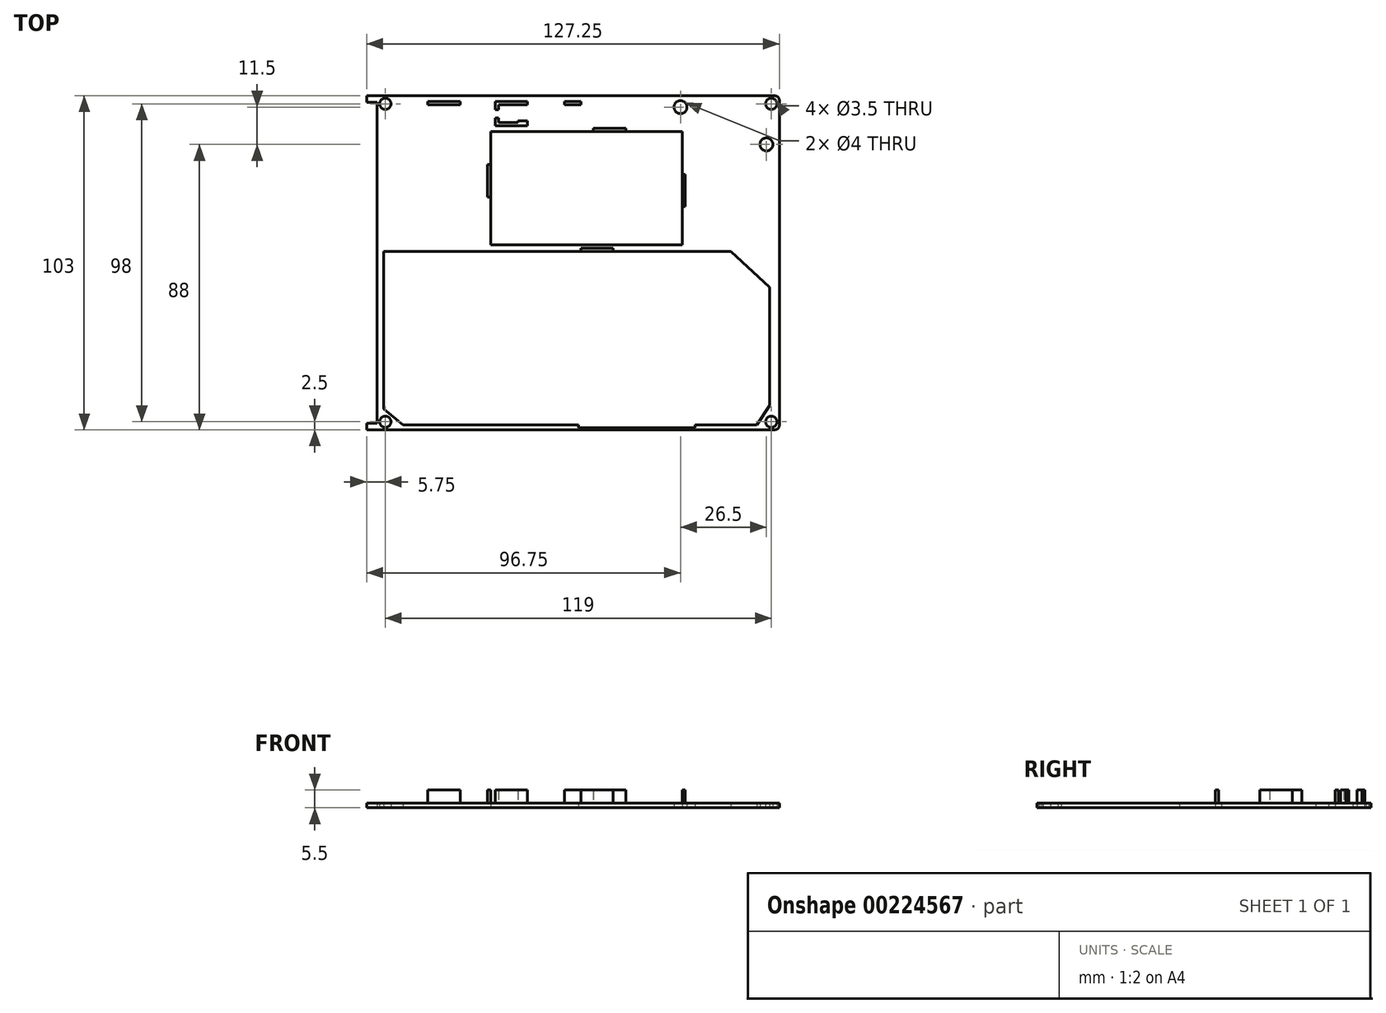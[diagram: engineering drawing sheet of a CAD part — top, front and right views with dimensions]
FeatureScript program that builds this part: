
annotation { "Feature Type Name" : "Feature", "Feature Type Description" : "" }
export const myFeature = defineFeature(function(context is Context, id is Id, definition is map)
    precondition{}
    {
        {
            var Q0;
            Q0=qCreatedBy(makeId("Top.planeOp"),FACE);
            var sketch = newSketch(context, id + "F0", { "sketchPlane" : qUnion([Q0])});
            skLineSegment(sketch, "E0.bottom", {"start": v(-1.5, 0) * mm, "end": v(-122.5, 0) * mm});
            skLineSegment(sketch, "E0.top", {"start": v(-1.5, 103) * mm, "end": v(-122.5, 103) * mm});
            skLineSegment(sketch, "E0.left", {"start": v(0, 1.5) * mm, "end": v(0, 101.5) * mm});
            skLineSegment(sketch, "E0.right", {"start": v(-124, 2) * mm, "end": v(-124, 101) * mm});
            skLineSegment(sketch, "E1.bottom", {"start": v(-7, 1.5) * mm, "end": v(-116, 1.5) * mm});
            skLineSegment(sketch, "E1.top", {"start": v(-30, 92) * mm, "end": v(-89, 92) * mm});
            skLineSegment(sketch, "E1.left", {"start": v(-3, 7.5) * mm, "end": v(-3, 44) * mm});
            skLineSegment(sketch, "E1.right", {"start": v(-122, 6.5) * mm, "end": v(-122, 55) * mm});
            skLineSegment(sketch, "E2", {"start": v(-116, 1.5) * mm, "end": v(-122, 6.5) * mm});
            skLineSegment(sketch, "E3", {"start": v(-7, 1.5) * mm, "end": v(-3, 7.5) * mm});
            skLineSegment(sketch, "E4", {"start": v(-3, 44) * mm, "end": v(-15, 55) * mm});
            skLineSegment(sketch, "E5", {"start": v(-15, 55) * mm, "end": v(-30, 55) * mm});
            skLineSegment(sketch, "E6", {"start": v(-30, 57) * mm, "end": v(-30, 92) * mm});
            skLineSegment(sketch, "E7", {"start": v(-30, 55) * mm, "end": v(-122, 55) * mm});
            skLineSegment(sketch, "E8", {"start": v(-30, 57) * mm, "end": v(-89, 57) * mm});
            skLineSegment(sketch, "E9", {"start": v(-89, 92) * mm, "end": v(-89, 57) * mm});
            skCircle(sketch, "E10", {"center": v(-2.5, 100.5) * mm, "radius": 1.75 * mm});
            skCircle(sketch, "E11", {"center": v(-121.5, 100.5) * mm, "radius": 1.75 * mm});
            skCircle(sketch, "E12", {"center": v(-121.5, 2.5) * mm, "radius": 1.75 * mm});
            skCircle(sketch, "E13", {"center": v(-2.5, 2.5) * mm, "radius": 1.75 * mm});
            skCircle(sketch, "E14", {"center": v(-4, 88) * mm, "radius": 2 * mm});
            skCircle(sketch, "E15", {"center": v(-30.5, 99.5) * mm, "radius": 2 * mm});
            skPoint(sketch, "E16.visualSharp", {"position": v(0, 103) * mm});
            skArc(sketch, "E16.filletArc", {"start": v(0, 101.5) * mm, "mid": v(-0.44, 102.56) * mm, "end": v(-1.5, 103) * mm});
            skPoint(sketch, "E17.visualSharp", {"position": v(0, 0) * mm});
            skArc(sketch, "E17.filletArc", {"start": v(-1.5, 0) * mm, "mid": v(-0.44, 0.44) * mm, "end": v(0, 1.5) * mm});
            skLineSegment(sketch, "E18", {"start": v(-26, 1.5) * mm, "end": v(-26, 0.7) * mm});
            skLineSegment(sketch, "E19", {"start": v(-26, 0.7) * mm, "end": v(-62, 0.7) * mm});
            skLineSegment(sketch, "E20", {"start": v(-62, 0.7) * mm, "end": v(-62, 1.5) * mm});
            skLineSegment(sketch, "E21", {"start": v(-124, 2) * mm, "end": v(-127.25, 2) * mm});
            skLineSegment(sketch, "E22", {"start": v(-127.25, 2) * mm, "end": v(-127.25, 0) * mm});
            skLineSegment(sketch, "E23", {"start": v(-127.25, 0) * mm, "end": v(-122.5, 0) * mm});
            skLineSegment(sketch, "E24", {"start": v(-122.5, 103) * mm, "end": v(-127.25, 103) * mm});
            skLineSegment(sketch, "E25", {"start": v(-124, 101) * mm, "end": v(-127.25, 101) * mm});
            skLineSegment(sketch, "E26", {"start": v(-127.25, 101) * mm, "end": v(-127.25, 103) * mm});
            skSolve(sketch);
        }
        {
            var Q0;
            Q0 = qSketchRegion(id + "F0", true);
            extrude(context, id + "F1", {"entities" : qUnion([Q0]), "depth" : 1.5 * mm});
        }
        {
            var Q0;
            Q0=makeQuery(id+"F1.opExtrude","CAP_FACE",FACE,{"disambiguationData":[OSD([sQuery(id+"F0.wireOp",EDGE,"E0.bottom"),sQuery(id+"F0.wireOp",EDGE,"E0.top"),sQuery(id+"F0.wireOp",EDGE,"E0.left"),sQuery(id+"F0.wireOp",EDGE,"E0.right"),sQuery(id+"F0.wireOp",EDGE,"E1.bottom"),sQuery(id+"F0.wireOp",EDGE,"E1.top"),sQuery(id+"F0.wireOp",EDGE,"E1.left"),sQuery(id+"F0.wireOp",EDGE,"E1.right"),sQuery(id+"F0.wireOp",EDGE,"E2"),sQuery(id+"F0.wireOp",EDGE,"E3"),sQuery(id+"F0.wireOp",EDGE,"E4"),sQuery(id+"F0.wireOp",EDGE,"E5"),sQuery(id+"F0.wireOp",EDGE,"E6"),sQuery(id+"F0.wireOp",EDGE,"E7"),sQuery(id+"F0.wireOp",EDGE,"E8"),sQuery(id+"F0.wireOp",EDGE,"E9"),sQuery(id+"F0.wireOp",EDGE,"E10"),sQuery(id+"F0.wireOp",EDGE,"E11"),sQuery(id+"F0.wireOp",EDGE,"E12"),sQuery(id+"F0.wireOp",EDGE,"E13"),sQuery(id+"F0.wireOp",EDGE,"E14"),sQuery(id+"F0.wireOp",EDGE,"E15"),sQuery(id+"F0.wireOp",EDGE,"E16.filletArc"),sQuery(id+"F0.wireOp",EDGE,"E17.filletArc"),sQuery(id+"F0.wireOp",EDGE,"009ea5dd-0bb8-4e20-ba9f-81f578676786.filletArc"),sQuery(id+"F0.wireOp",EDGE,"e55fcb94-b343-4f6b-ae36-d151259c01dc.filletArc"),sQuery(id+"F0.wireOp",EDGE,"E18"),sQuery(id+"F0.wireOp",EDGE,"E19"),sQuery(id+"F0.wireOp",EDGE,"E20")])],"isStart":false});
            var sketch = newSketch(context, id + "F2", { "sketchPlane" : qUnion([Q0])});
            skLineSegment(sketch, "E27.bottom", {"start": v(-87.63, 101.2) * mm, "end": v(-77.63, 101.2) * mm});
            skLineSegment(sketch, "E27.top", {"start": v(-86.63, 100.2) * mm, "end": v(-77.63, 100.2) * mm});
            skLineSegment(sketch, "E27.left", {"start": v(-87.63, 101.2) * mm, "end": v(-87.63, 100.2) * mm});
            skLineSegment(sketch, "E27.right", {"start": v(-77.63, 101.2) * mm, "end": v(-77.63, 100.2) * mm});
            skLineSegment(sketch, "E28.top", {"start": v(-87.63, 98.7) * mm, "end": v(-86.63, 98.7) * mm});
            skLineSegment(sketch, "E28.left", {"start": v(-87.63, 100.2) * mm, "end": v(-87.63, 98.7) * mm});
            skLineSegment(sketch, "E28.right", {"start": v(-86.63, 100.2) * mm, "end": v(-86.63, 98.7) * mm});
            skLineSegment(sketch, "E29.bottom", {"start": v(-87.63, 96.2) * mm, "end": v(-86.63, 96.2) * mm});
            skLineSegment(sketch, "E29.left", {"start": v(-87.63, 96.2) * mm, "end": v(-87.63, 94.7) * mm});
            skLineSegment(sketch, "E29.right", {"start": v(-86.63, 96.2) * mm, "end": v(-86.63, 94.7) * mm});
            skLineSegment(sketch, "E30.bottom", {"start": v(-86.63, 94.7) * mm, "end": v(-80.63, 94.7) * mm});
            skLineSegment(sketch, "E30.top", {"start": v(-87.63, 93.7) * mm, "end": v(-77.63, 93.7) * mm});
            skLineSegment(sketch, "E30.left", {"start": v(-87.63, 94.7) * mm, "end": v(-87.63, 93.7) * mm});
            skLineSegment(sketch, "E30.right", {"start": v(-77.63, 94.7) * mm, "end": v(-77.63, 93.7) * mm});
            skLineSegment(sketch, "E31.top", {"start": v(-77.63, 95.25) * mm, "end": v(-80.63, 95.25) * mm});
            skLineSegment(sketch, "E31.left", {"start": v(-77.63, 94.7) * mm, "end": v(-77.63, 95.25) * mm});
            skLineSegment(sketch, "E31.right", {"start": v(-80.63, 94.7) * mm, "end": v(-80.63, 95.25) * mm});
            skLineSegment(sketch, "E32.bottom", {"start": v(-89, 81.76) * mm, "end": v(-90, 81.76) * mm});
            skLineSegment(sketch, "E32.top", {"start": v(-89, 71.76) * mm, "end": v(-90, 71.76) * mm});
            skLineSegment(sketch, "E32.left", {"start": v(-89, 81.76) * mm, "end": v(-89, 71.76) * mm});
            skLineSegment(sketch, "E32.right", {"start": v(-90, 81.76) * mm, "end": v(-90, 71.76) * mm});
            skLineSegment(sketch, "E33.bottom", {"start": v(-61.21, 55) * mm, "end": v(-51.21, 55) * mm});
            skLineSegment(sketch, "E33.top", {"start": v(-61.21, 56) * mm, "end": v(-51.21, 56) * mm});
            skLineSegment(sketch, "E33.left", {"start": v(-61.21, 55) * mm, "end": v(-61.21, 56) * mm});
            skLineSegment(sketch, "E33.right", {"start": v(-51.21, 55) * mm, "end": v(-51.21, 56) * mm});
            skLineSegment(sketch, "E34.bottom", {"start": v(-30, 68.8) * mm, "end": v(-29, 68.8) * mm});
            skLineSegment(sketch, "E34.top", {"start": v(-30, 78.8) * mm, "end": v(-29, 78.8) * mm});
            skLineSegment(sketch, "E34.left", {"start": v(-30, 68.8) * mm, "end": v(-30, 78.8) * mm});
            skLineSegment(sketch, "E34.right", {"start": v(-29, 68.8) * mm, "end": v(-29, 78.8) * mm});
            skLineSegment(sketch, "E35.bottom", {"start": v(-57.37, 92) * mm, "end": v(-47.37, 92) * mm});
            skLineSegment(sketch, "E35.top", {"start": v(-57.37, 93) * mm, "end": v(-47.37, 93) * mm});
            skLineSegment(sketch, "E35.left", {"start": v(-57.37, 92) * mm, "end": v(-57.37, 93) * mm});
            skLineSegment(sketch, "E35.right", {"start": v(-47.37, 92) * mm, "end": v(-47.37, 93) * mm});
            skLineSegment(sketch, "E36.bottom", {"start": v(-108.4, 101.2) * mm, "end": v(-98.4, 101.2) * mm});
            skLineSegment(sketch, "E36.top", {"start": v(-108.4, 100.2) * mm, "end": v(-98.4, 100.2) * mm});
            skLineSegment(sketch, "E36.left", {"start": v(-108.4, 101.2) * mm, "end": v(-108.4, 100.2) * mm});
            skLineSegment(sketch, "E36.right", {"start": v(-98.4, 101.2) * mm, "end": v(-98.4, 100.2) * mm});
            skLineSegment(sketch, "E37.bottom", {"start": v(-66.23, 101.2) * mm, "end": v(-61.23, 101.2) * mm});
            skLineSegment(sketch, "E37.top", {"start": v(-66.23, 100.2) * mm, "end": v(-61.23, 100.2) * mm});
            skLineSegment(sketch, "E37.left", {"start": v(-66.23, 101.2) * mm, "end": v(-66.23, 100.2) * mm});
            skLineSegment(sketch, "E37.right", {"start": v(-61.23, 101.2) * mm, "end": v(-61.23, 100.2) * mm});
            skSolve(sketch);
        }
        {
            var Q0;
            Q0 = qSketchRegion(id + "F2", true);
            extrude(context, id + "F3", {"entities" : qUnion([Q0]), "operationType" : NewBodyOperationType.ADD, "depth" : 4 * mm});
        }
    });
